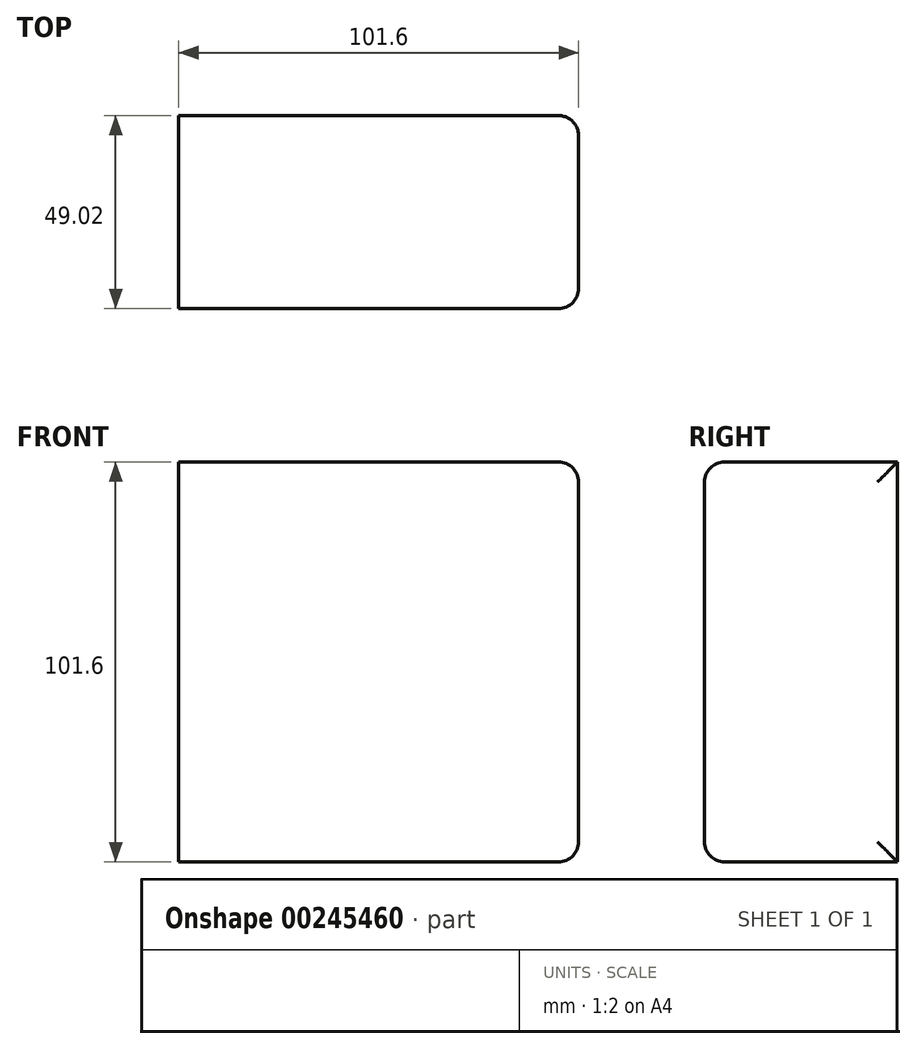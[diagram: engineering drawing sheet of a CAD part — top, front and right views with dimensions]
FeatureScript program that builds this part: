
annotation { "Feature Type Name" : "Feature", "Feature Type Description" : "" }
export const myFeature = defineFeature(function(context is Context, id is Id, definition is map)
    precondition{}
    {
        {
            var Q0;
            Q0=qCreatedBy(makeId("Front.planeOp"),FACE);
            var sketch = newSketch(context, id + "F0", { "sketchPlane" : qUnion([Q0])});
            skLineSegment(sketch, "E0.bottom", {"start": v(-50.8, 50.8) * mm, "end": v(50.8, 50.8) * mm});
            skLineSegment(sketch, "E0.top", {"start": v(-50.8, -50.8) * mm, "end": v(50.8, -50.8) * mm});
            skLineSegment(sketch, "E0.left", {"start": v(-50.8, 50.8) * mm, "end": v(-50.8, -50.8) * mm});
            skLineSegment(sketch, "E0.right", {"start": v(50.8, 50.8) * mm, "end": v(50.8, -50.8) * mm});
            skSolve(sketch);
        }
        {
            var Q0;
            Q0=makeQuery(id+"F0.imprint","IMPRINT",FACE,{"disambiguationData":[TD([[makeQuery(id+"F0.imprint","IMPRINT",EDGE,{"derivedFrom":sQuery(id+"F0.wireOp",EDGE,"E0.bottom")}),-1.0]])]});
            extrude(context, id + "F1", {"entities" : qUnion([Q0]), "depth" : 23.62 * mm, "hasSecondDirection" : true, "secondDirectionOppositeDirection" : true, "secondDirectionDepth" : 25.4 * mm});
        }
        {
            var Q0;
            Q0=makeQuery(id+"F1.opExtrude","CAP_EDGE",EDGE,{"disambiguationData":[OSD([sQuery(id+"F0.wireOp",EDGE,"E0.bottom")])],"isStart":false});
            var Q1;
            Q1=makeQuery(id+"F1.opExtrude","SWEPT_FACE",FACE,{"disambiguationData":[OSD([sQuery(id+"F0.wireOp",EDGE,"E0.right")])]});
            var Q2;
            Q2=makeQuery(id+"F1.opExtrude","CAP_EDGE",EDGE,{"disambiguationData":[OSD([sQuery(id+"F0.wireOp",EDGE,"E0.top")])],"isStart":false});
            fillet(context, id + "F2", {"entities" : qUnion([Q0, Q1, Q2]), "radius" : 5.08 * mm, "tangentPropagation" : true, "allowEdgeOverflow" : false});
        }
    });
